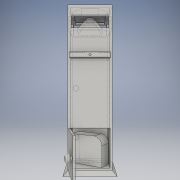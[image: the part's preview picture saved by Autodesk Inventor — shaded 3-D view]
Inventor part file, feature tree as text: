
AUTODESK INVENTOR PART (.ipt)
format: ipt  version: 2016 (Build 200138000, 138)  size: 382,464 bytes
history: native  units: in
note: dims shown in document units (in); Inventor stores cm internally (conversion verified against a paired STEP export)
features: sketch x23, extrude x21, fillet x2, chamfer x1, plane x1, loft x1
ambient origin geometry x8: Origin, YZ Plane, XZ Plane, XY Plane, X Axis, Y Axis, Z Axis, Center Point
bodies: Solid1 (feature_tree)
feature tree (49):
  extrude  "Extrusion1"  Depth=16.0in TaperAngle=0.0deg
  extrude  "Extrusion2"  Depth=2.0in TaperAngle=0.0deg
  extrude  "Extrusion3"  Depth=18.0in TaperAngle=0.0deg
  extrude  "Extrusion4"  Depth=2.0in
  chamfer  "Chamfer1"  Angle=90.0deg  [1 undecoded]
  sketch  "Sketch5"  dims[d33=6.5in]
  plane  "Work Plane1"
  loft  "Loft1"
  extrude  "Extrusion5"  Depth=2.56in TaperAngle=0.0deg
  extrude  "Extrusion6"  Depth=0.94in
  extrude  "Extrusion7"  Depth=1.5in
  extrude  "Extrusion8"  Depth=1.5in
  extrude  "Extrusion9"  Depth=5.5in TaperAngle=0.0deg
  extrude  "Extrusion10"  Depth=1.25in
  extrude  "Extrusion11"  Depth=1.25in
  extrude  "Extrusion12"  Depth=1.25in
  fillet  "Fillet1"  Radius=1.0in
  extrude  "Extrusion13"  Depth=18.0in
  extrude  "Extrusion14"  Depth=1.0in
  extrude  "Extrusion15"  Depth=1.0in
  extrude  "Extrusion16"  Depth=2.8in TaperAngle=0.0deg
  extrude  "Extrusion17"  Depth=16.0in TaperAngle=0.0deg
  extrude  "Extrusion18"  Depth=16.5in
  extrude  "Extrusion19"  Depth=4.125in
  fillet  "Fillet2"  Radius=12.0in
  extrude  "Extrusion20"  Depth=2.8in
  extrude  "Extrusion21"  Depth=1.0in
  sketch  "Sketch1"  dims[d0=64.0in d1=20.0in d3=1.0in d4=1.0in d5=1.0in d6=1.0in d7=2.0in d8=2.0in d19=2.0in d20=16.0in d21=0.0in]
  sketch  "Sketch2"  dims[d22=2.0in d23=0.0in d24=2.0in d25=0.0in]
  sketch  "Sketch3"  dims[d26=1.0in d27=18.0in d28=0.0in]
  sketch  "Sketch4"  dims[d29=2.0in d30=0.125in d31=45.0deg d32=11.75in]
  sketch  "Sketch6"  dims[d34=2.5in d35=0.0in d36=90.0deg]
  sketch  "Sketch7"  dims[d37=0.0in d38=90.0deg d39=13.3in]
  sketch  "Sketch8"  dims[d40=16.2in d41=2.56in d42=0.0in]
  sketch  "Sketch9"  dims[d49=8.1in d50=0.94in]
  sketch  "Sketch10"  dims[d51=25.565in d52=0.0in d53=1.5in]
  sketch  "Sketch11"  dims[d54=1.5in d55=1.5in]
  sketch  "Sketch12"  dims[d56=1.5in d57=5.5in d58=0.0in]
  sketch  "Sketch13"  dims[d59=1.25in d60=1.25in]
  sketch  "Sketch14"  dims[d61=1.25in d62=1.25in]
  sketch  "Sketch16"  dims[d63=1.25in d64=1.25in d65=1.0in d66=0.0in]
  sketch  "Sketch17"  dims[d67=1.0in d68=18.0in]
  sketch  "Sketch18"  dims[d69=18.0in d70=0.0in d71=1.0in]
  sketch  "Sketch19"  dims[d72=1.0in d73=1.0in]
  sketch  "Sketch20"  dims[d74=1.0in d76=2.8in d77=0.0in]
  sketch  "Sketch21"  dims[d78=1.0in d79=16.0in d80=0.0in]
  sketch  "Sketch22"  dims[d81=6.75in d82=16.5in]
  sketch  "Sketch23"  dims[d83=14.0in d84=0.0in d85=4.125in d95=12.0in]
  sketch  "Sketch24"  dims[d96=3.0in d99=2.8in d100=37.0in d101=1.625in d102=0.0in d104=2.5in d105=3.875in d106=0.0in d107=0.5in d108=10.5in d109=0.0in d111=0.5in d112=0.0in d113=18.0in d114=11.0in d115=0.5in d116=18.0in d117=1.0in d118=18.0in d119=0.0in d120=1.5in d121=0.75in d122=0.0in d123=4.0in d124=2.0in d125=0.0in d126=1.0in d127=3.0in d128=0.0in d129=0.5in d130=1.8in d131=0.0in d132=1.0in d133=1.3125in d134=0.0in d135=2.0in d136=2.8in d86=1.0in d87=1.0in]
note: 1 required parameter value undecoded (feature->parameter linkage not recoverable at this tier; creation-order binding heuristic only, values carry confidence <= 0.55)
